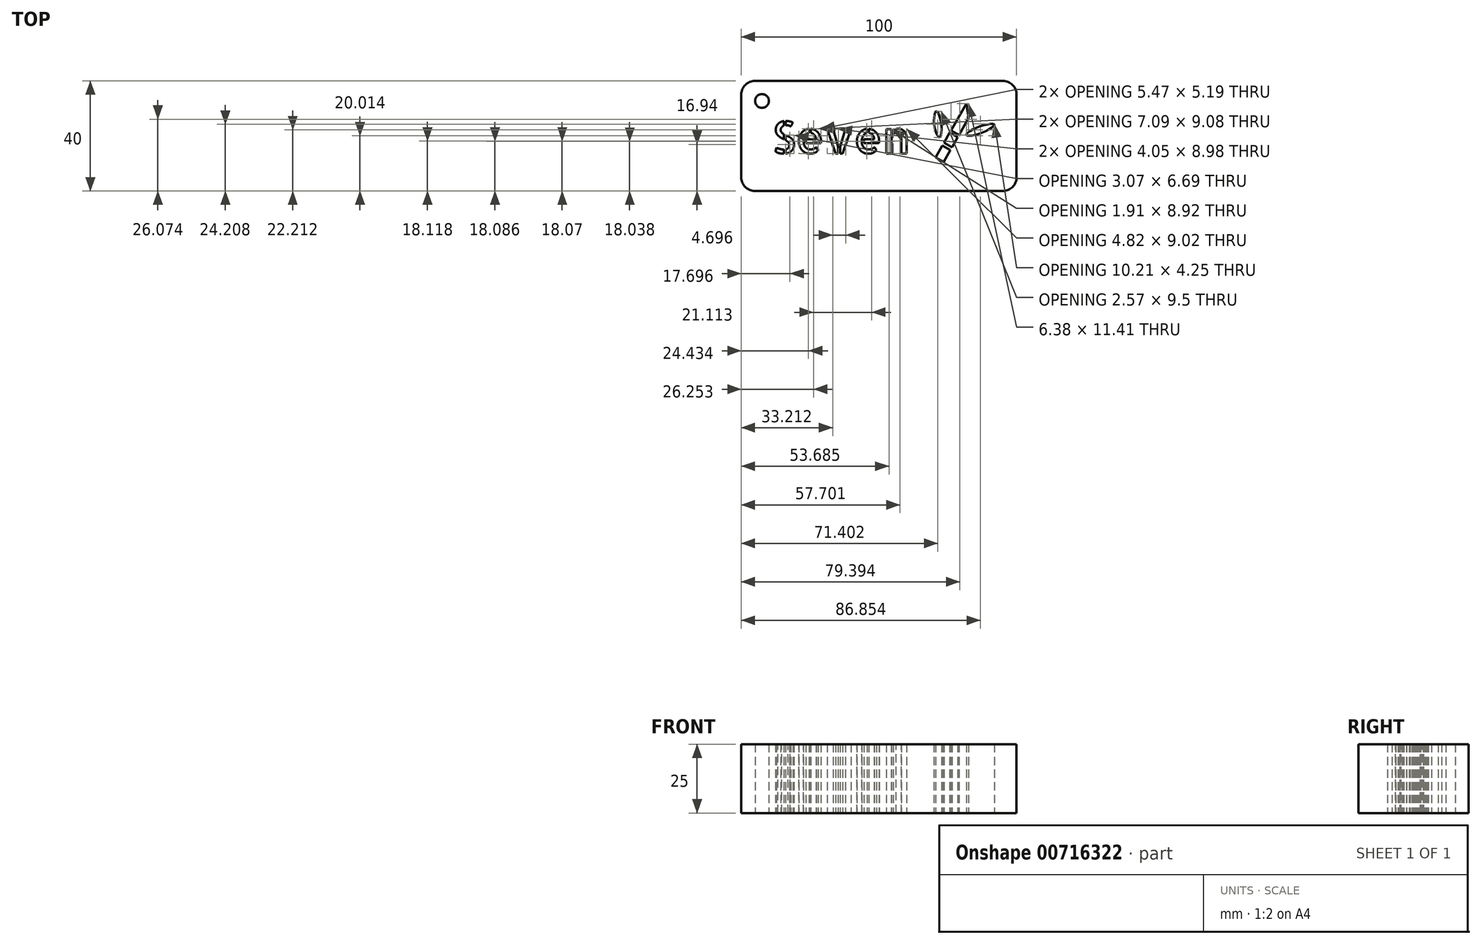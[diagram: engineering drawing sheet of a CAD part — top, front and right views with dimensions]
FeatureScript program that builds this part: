
annotation { "Feature Type Name" : "Feature", "Feature Type Description" : "" }
export const myFeature = defineFeature(function(context is Context, id is Id, definition is map)
    precondition{}
    {
        {
            var Q0;
            Q0=qCreatedBy(makeId("Top.planeOp"),FACE);
            var sketch = newSketch(context, id + "F0", { "sketchPlane" : qUnion([Q0])});
            skLineSegment(sketch, "E0.bottom", {"start": v(5, 0) * mm, "end": v(95, 0) * mm});
            skLineSegment(sketch, "E0.top", {"start": v(5, 40) * mm, "end": v(95, 40) * mm});
            skLineSegment(sketch, "E0.left", {"start": v(0, 5) * mm, "end": v(0, 35) * mm});
            skLineSegment(sketch, "E0.right", {"start": v(100, 5) * mm, "end": v(100, 35) * mm});
            skCircle(sketch, "E1", {"center": v(7.55, 32.71) * mm, "radius": 2.5 * mm});
            skPoint(sketch, "E2.visualSharp", {"position": v(0, 40) * mm});
            skArc(sketch, "E2.filletArc", {"start": v(5, 40) * mm, "mid": v(1.46, 38.54) * mm, "end": v(0, 35) * mm});
            skPoint(sketch, "E3.visualSharp", {"position": v(0, 0) * mm});
            skArc(sketch, "E3.filletArc", {"start": v(0, 5) * mm, "mid": v(1.46, 1.46) * mm, "end": v(5, 0) * mm});
            skPoint(sketch, "E4.visualSharp", {"position": v(100, 0) * mm});
            skArc(sketch, "E4.filletArc", {"start": v(95, 0) * mm, "mid": v(98.54, 1.46) * mm, "end": v(100, 5) * mm});
            skPoint(sketch, "E5.visualSharp", {"position": v(100, 40) * mm});
            skArc(sketch, "E5.filletArc", {"start": v(100, 35) * mm, "mid": v(98.54, 38.54) * mm, "end": v(95, 40) * mm});
            skText(sketch, "E6", { "text": "Seven", "fontName": "AllertaStencil-Regular.ttf"});
            skLineSegment(sketch, "E7", {"start": v(70.66, 12.24) * mm, "end": v(73.08, 16.5) * mm});
            skLineSegment(sketch, "E8", {"start": v(70.66, 12.24) * mm, "end": v(73.54, 10.6) * mm});
            skLineSegment(sketch, "E9", {"start": v(73.54, 10.6) * mm, "end": v(75.96, 14.86) * mm});
            skLineSegment(sketch, "E10", {"start": v(82.58, 26.53) * mm, "end": v(81.75, 31.78) * mm});
            skFitSpline(sketch, "E11", {"points": [v(81.75, 20.34) * mm, v(85.8, 23.15) * mm, v(91.96, 24.2) * mm, v(86.68, 20.86) * mm, v(81.75, 20.34) * mm]});
            skFitSpline(sketch, "E12", {"points": [v(72.07, 19.46) * mm, v(72.6, 24.56) * mm, v(70.83, 28.96) * mm, v(70.13, 23.86) * mm, v(72.07, 19.46) * mm]});
            skLineSegment(sketch, "E13", {"start": v(76.2, 22) * mm, "end": v(79.09, 20.37) * mm});
            skLineSegment(sketch, "E14", {"start": v(75.74, 21.19) * mm, "end": v(78.62, 19.55) * mm});
            skLineSegment(sketch, "E15.trimOffspring", {"start": v(79.09, 20.37) * mm, "end": v(82.58, 26.53) * mm});
            skLineSegment(sketch, "E16.trimOffspring", {"start": v(76.2, 22) * mm, "end": v(81.75, 31.78) * mm});
            skLineSegment(sketch, "E17", {"start": v(73.64, 17.5) * mm, "end": v(76.53, 15.86) * mm});
            skLineSegment(sketch, "E18", {"start": v(73.08, 16.5) * mm, "end": v(75.96, 14.86) * mm});
            skLineSegment(sketch, "E19.trimOffspring", {"start": v(76.53, 15.86) * mm, "end": v(78.62, 19.55) * mm});
            skLineSegment(sketch, "E20.trimOffspring", {"start": v(73.64, 17.5) * mm, "end": v(75.74, 21.19) * mm});
            const initialGuessF0  = {"E6": [0.01118, 0.01361, 1, 0, 0.01166]};
            skSetInitialGuess(sketch, initialGuessF0);
            skSolve(sketch);
        }
        {
            var Q0;
            Q0 = qSketchRegion(id + "F0", true);
            extrude(context, id + "F1", {"entities" : qUnion([Q0]), "depth" : 25 * mm, "offsetDistance" : 25 * mm});
        }
        {
            var Q0;
            Q0 = qSketchRegion(id + "F0", true);
            extrude(context, id + "F2", {"entities" : qUnion([Q0]), "operationType" : NewBodyOperationType.ADD, "depth" : 25 * mm, "offsetDistance" : 25 * mm});
        }
    });
